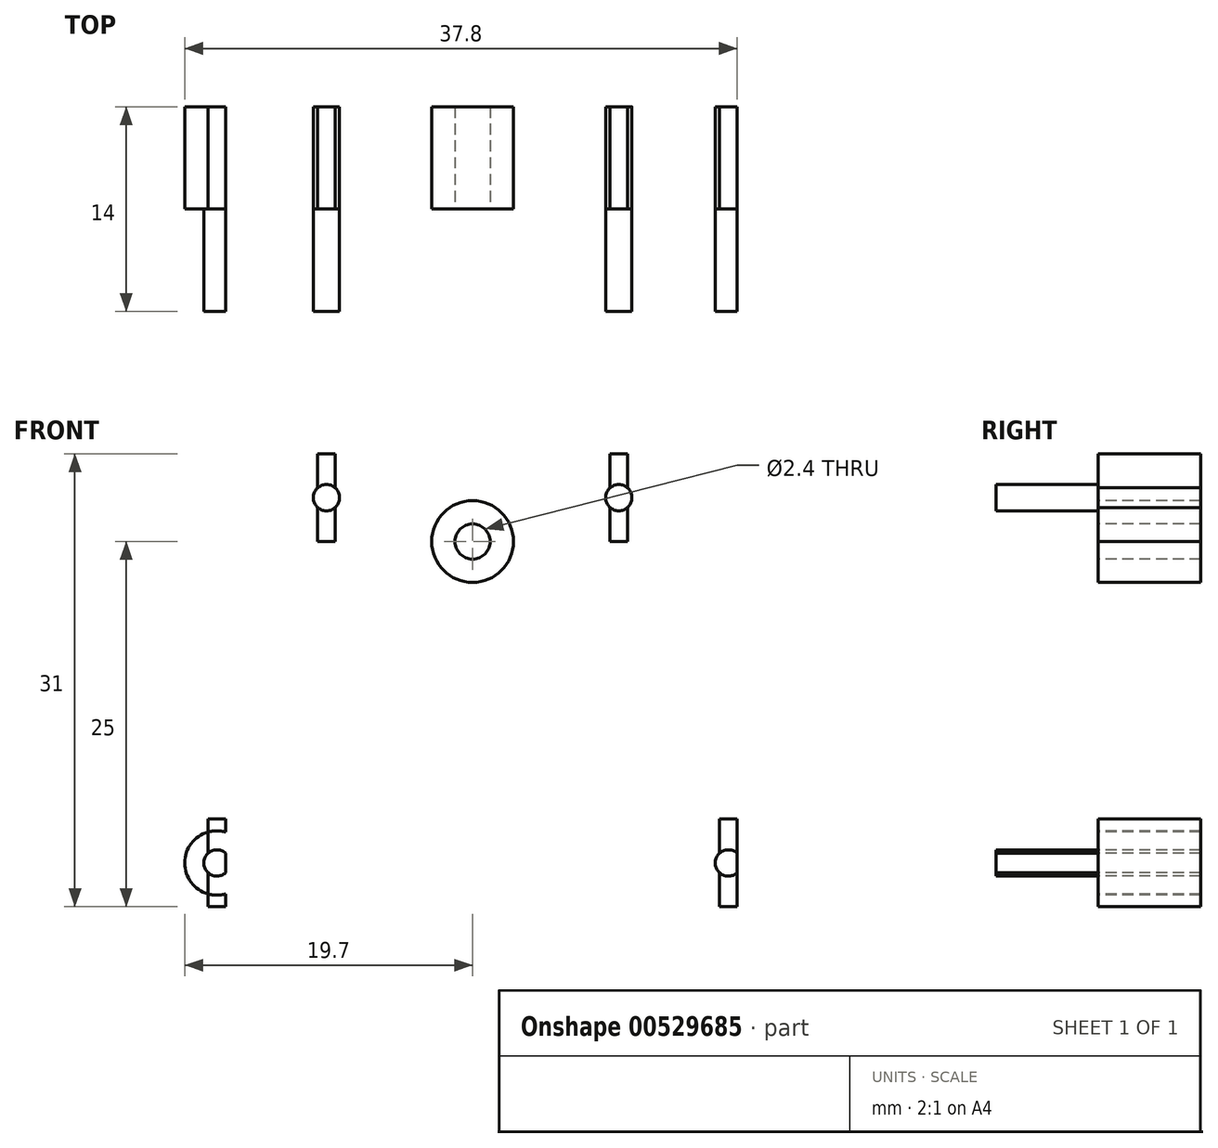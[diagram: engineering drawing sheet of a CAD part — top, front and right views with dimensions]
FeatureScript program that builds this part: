
annotation { "Feature Type Name" : "Feature", "Feature Type Description" : "" }
export const myFeature = defineFeature(function(context is Context, id is Id, definition is map)
    precondition{}
    {
        {
            var Q0;
            Q0=qCreatedBy(makeId("Front.planeOp"),FACE);
            var sketch = newSketch(context, id + "F0", { "sketchPlane" : qUnion([Q0])});
            skLineSegment(sketch, "E0", {"start": v(7.5, 25) * mm, "end": v(27.5, 25) * mm, "construction": true});
            skLineSegment(sketch, "E1", {"start": v(0, 0) * mm, "end": v(35, 0) * mm, "construction": true});
            skLineSegment(sketch, "E2", {"start": v(35, 0) * mm, "end": v(27.5, 25) * mm, "construction": true});
            skLineSegment(sketch, "E3", {"start": v(7.5, 25) * mm, "end": v(0, 0) * mm, "construction": true});
            skLineSegment(sketch, "E4", {"start": v(17.5, 25) * mm, "end": v(17.5, 0) * mm, "construction": true});
            skPoint(sketch, "E4.endSnap0", {"position": v(17.5, 0) * mm});
            skCircle(sketch, "E5", {"center": v(7.5, 25) * mm, "radius": 0.9 * mm});
            skCircle(sketch, "E6", {"center": v(27.5, 25) * mm, "radius": 0.9 * mm});
            skCircle(sketch, "E7", {"center": v(35, 0) * mm, "radius": 0.9 * mm});
            skCircle(sketch, "E8", {"center": v(0, 0) * mm, "radius": 0.9 * mm});
            skCircle(sketch, "E9", {"center": v(17.5, 22) * mm, "radius": 1.2 * mm});
            skCircle(sketch, "E10", {"center": v(17.5, 22) * mm, "radius": 2.8 * mm});
            skLineSegment(sketch, "E11.bottom", {"start": v(8.1, 22) * mm, "end": v(6.9, 22) * mm});
            skLineSegment(sketch, "E11.top", {"start": v(8.1, 28) * mm, "end": v(6.9, 28) * mm});
            skLineSegment(sketch, "E11.left", {"start": v(8.1, 22) * mm, "end": v(8.1, 28) * mm});
            skLineSegment(sketch, "E11.right", {"start": v(6.9, 22) * mm, "end": v(6.9, 28) * mm});
            skLineSegment(sketch, "E12.bottom", {"start": v(28.1, 22) * mm, "end": v(26.9, 22) * mm});
            skLineSegment(sketch, "E12.top", {"start": v(28.1, 28) * mm, "end": v(26.9, 28) * mm});
            skLineSegment(sketch, "E12.left", {"start": v(28.1, 22) * mm, "end": v(28.1, 28) * mm});
            skLineSegment(sketch, "E12.right", {"start": v(26.9, 22) * mm, "end": v(26.9, 28) * mm});
            skLineSegment(sketch, "E13.bottom", {"start": v(35.6, 3) * mm, "end": v(34.4, 3) * mm});
            skLineSegment(sketch, "E13.top", {"start": v(35.6, -3) * mm, "end": v(34.4, -3) * mm});
            skLineSegment(sketch, "E13.left", {"start": v(35.6, 3) * mm, "end": v(35.6, -3) * mm});
            skLineSegment(sketch, "E13.right", {"start": v(34.4, 3) * mm, "end": v(34.4, -3) * mm});
            skLineSegment(sketch, "E14.bottom", {"start": v(-0.6, 3) * mm, "end": v(0.6, 3) * mm});
            skLineSegment(sketch, "E14.top", {"start": v(-0.6, -3) * mm, "end": v(0.6, -3) * mm});
            skLineSegment(sketch, "E14.left", {"start": v(-0.6, 3) * mm, "end": v(-0.6, -3) * mm});
            skLineSegment(sketch, "E14.right", {"start": v(0.6, 3) * mm, "end": v(0.6, -3) * mm});
            skPoint(sketch, "E14.cornerSnap0", {"position": v(35, 3) * mm});
            skCircle(sketch, "E15", {"center": v(7.5, 25) * mm, "radius": 2.2 * mm});
            skCircle(sketch, "E16", {"center": v(27.5, 25) * mm, "radius": 2.2 * mm});
            skCircle(sketch, "E17", {"center": v(35, 0) * mm, "radius": 2.2 * mm});
            skCircle(sketch, "E18", {"center": v(0, 0) * mm, "radius": 2.2 * mm});
            skCircle(sketch, "E19", {"center": v(17.5, 4) * mm, "radius": 0.6 * mm});
            skSolve(sketch);
        }
        {
            var Q0;
            {var subQ0=sQuery(id+"F0.wireOp",EDGE,"E11.right");var subQ1=sQuery(id+"F0.wireOp",EDGE,"E5");var subQ2=makeQuery(id+"F0.imprint","INTERSECT",VERTEX,{"disambiguationData":[OD(0.0)],"derivedFrom":[subQ1,subQ0]});Q0=makeQuery(id+"F0.imprint","IMPRINT",FACE,{"disambiguationData":[TD([[makeQuery(id+"F0.imprint","IMPRINT",EDGE,{"disambiguationData":[TD([[subQ2,1.0]])],"derivedFrom":subQ1}),1.0]])]});}
            var Q1;
            {var subQ0=sQuery(id+"F0.wireOp",EDGE,"E11.right");var subQ1=sQuery(id+"F0.wireOp",EDGE,"E5");var subQ2=makeQuery(id+"F0.imprint","INTERSECT",VERTEX,{"disambiguationData":[OD(0.0)],"derivedFrom":[subQ1,subQ0]});Q1=makeQuery(id+"F0.imprint","IMPRINT",FACE,{"disambiguationData":[TD([[makeQuery(id+"F0.imprint","IMPRINT",EDGE,{"disambiguationData":[TD([[subQ2,-1.0]])],"derivedFrom":subQ1}),1.0]])]});}
            var Q2;
            {var subQ0=sQuery(id+"F0.wireOp",EDGE,"E11.left");var subQ1=sQuery(id+"F0.wireOp",EDGE,"E5");var subQ2=makeQuery(id+"F0.imprint","INTERSECT",VERTEX,{"disambiguationData":[OD(0.0)],"derivedFrom":[subQ1,subQ0]});Q2=makeQuery(id+"F0.imprint","IMPRINT",FACE,{"disambiguationData":[TD([[makeQuery(id+"F0.imprint","IMPRINT",EDGE,{"disambiguationData":[TD([[subQ2,1.0]])],"derivedFrom":subQ1}),1.0]])]});}
            var Q3;
            {var subQ0=sQuery(id+"F0.wireOp",EDGE,"E12.right");var subQ1=sQuery(id+"F0.wireOp",EDGE,"E6");var subQ2=makeQuery(id+"F0.imprint","INTERSECT",VERTEX,{"disambiguationData":[OD(0.0)],"derivedFrom":[subQ1,subQ0]});Q3=makeQuery(id+"F0.imprint","IMPRINT",FACE,{"disambiguationData":[TD([[makeQuery(id+"F0.imprint","IMPRINT",EDGE,{"disambiguationData":[TD([[subQ2,1.0]])],"derivedFrom":subQ1}),1.0]])]});}
            var Q4;
            {var subQ0=sQuery(id+"F0.wireOp",EDGE,"E12.right");var subQ1=sQuery(id+"F0.wireOp",EDGE,"E6");var subQ2=makeQuery(id+"F0.imprint","INTERSECT",VERTEX,{"disambiguationData":[OD(0.0)],"derivedFrom":[subQ1,subQ0]});Q4=makeQuery(id+"F0.imprint","IMPRINT",FACE,{"disambiguationData":[TD([[makeQuery(id+"F0.imprint","IMPRINT",EDGE,{"disambiguationData":[TD([[subQ2,-1.0]])],"derivedFrom":subQ1}),1.0]])]});}
            var Q5;
            {var subQ0=sQuery(id+"F0.wireOp",EDGE,"E12.left");var subQ1=sQuery(id+"F0.wireOp",EDGE,"E6");var subQ2=makeQuery(id+"F0.imprint","INTERSECT",VERTEX,{"disambiguationData":[OD(0.0)],"derivedFrom":[subQ1,subQ0]});Q5=makeQuery(id+"F0.imprint","IMPRINT",FACE,{"disambiguationData":[TD([[makeQuery(id+"F0.imprint","IMPRINT",EDGE,{"disambiguationData":[TD([[subQ2,1.0]])],"derivedFrom":subQ1}),1.0]])]});}
            var Q6;
            {var subQ0=sQuery(id+"F0.wireOp",EDGE,"E13.right");var subQ1=sQuery(id+"F0.wireOp",EDGE,"E7");var subQ2=makeQuery(id+"F0.imprint","INTERSECT",VERTEX,{"disambiguationData":[OD(0.0)],"derivedFrom":[subQ1,subQ0]});Q6=makeQuery(id+"F0.imprint","IMPRINT",FACE,{"disambiguationData":[TD([[makeQuery(id+"F0.imprint","IMPRINT",EDGE,{"disambiguationData":[TD([[subQ2,1.0]])],"derivedFrom":subQ1}),1.0]])]});}
            var Q7;
            {var subQ0=sQuery(id+"F0.wireOp",EDGE,"E13.left");var subQ1=sQuery(id+"F0.wireOp",EDGE,"E7");var subQ2=makeQuery(id+"F0.imprint","INTERSECT",VERTEX,{"disambiguationData":[OD(0.0)],"derivedFrom":[subQ1,subQ0]});Q7=makeQuery(id+"F0.imprint","IMPRINT",FACE,{"disambiguationData":[TD([[makeQuery(id+"F0.imprint","IMPRINT",EDGE,{"disambiguationData":[TD([[subQ2,1.0]])],"derivedFrom":subQ1}),1.0]])]});}
            var Q8;
            {var subQ0=sQuery(id+"F0.wireOp",EDGE,"E13.right");var subQ1=sQuery(id+"F0.wireOp",EDGE,"E7");var subQ2=makeQuery(id+"F0.imprint","INTERSECT",VERTEX,{"disambiguationData":[OD(0.0)],"derivedFrom":[subQ1,subQ0]});Q8=makeQuery(id+"F0.imprint","IMPRINT",FACE,{"disambiguationData":[TD([[makeQuery(id+"F0.imprint","IMPRINT",EDGE,{"disambiguationData":[TD([[subQ2,-1.0]])],"derivedFrom":subQ1}),1.0]])]});}
            var Q9;
            {var subQ0=sQuery(id+"F0.wireOp",EDGE,"E14.left");var subQ1=sQuery(id+"F0.wireOp",EDGE,"E8");var subQ2=makeQuery(id+"F0.imprint","INTERSECT",VERTEX,{"disambiguationData":[OD(0.0)],"derivedFrom":[subQ1,subQ0]});Q9=makeQuery(id+"F0.imprint","IMPRINT",FACE,{"disambiguationData":[TD([[makeQuery(id+"F0.imprint","IMPRINT",EDGE,{"disambiguationData":[TD([[subQ2,-1.0]])],"derivedFrom":subQ1}),1.0]])]});}
            var Q10;
            {var subQ0=sQuery(id+"F0.wireOp",EDGE,"E14.left");var subQ1=sQuery(id+"F0.wireOp",EDGE,"E8");var subQ2=makeQuery(id+"F0.imprint","INTERSECT",VERTEX,{"disambiguationData":[OD(0.0)],"derivedFrom":[subQ1,subQ0]});Q10=makeQuery(id+"F0.imprint","IMPRINT",FACE,{"disambiguationData":[TD([[makeQuery(id+"F0.imprint","IMPRINT",EDGE,{"disambiguationData":[TD([[subQ2,1.0]])],"derivedFrom":subQ1}),1.0]])]});}
            var Q11;
            {var subQ0=sQuery(id+"F0.wireOp",EDGE,"E14.right");var subQ1=sQuery(id+"F0.wireOp",EDGE,"E8");var subQ2=makeQuery(id+"F0.imprint","INTERSECT",VERTEX,{"disambiguationData":[OD(0.0)],"derivedFrom":[subQ1,subQ0]});Q11=makeQuery(id+"F0.imprint","IMPRINT",FACE,{"disambiguationData":[TD([[makeQuery(id+"F0.imprint","IMPRINT",EDGE,{"disambiguationData":[TD([[subQ2,1.0]])],"derivedFrom":subQ1}),1.0]])]});}
            extrude(context, id + "F1", {"entities" : qUnion([Q0, Q1, Q2, Q3, Q4, Q5, Q6, Q7, Q8, Q9, Q10, Q11]), "depth" : 7 * mm, "offsetDistance" : 25 * mm});
        }
        {
            var Q0;
            Q0=makeQuery(id+"F0.imprint","IMPRINT",FACE,{"disambiguationData":[TD([[makeQuery(id+"F0.imprint","IMPRINT",EDGE,{"derivedFrom":sQuery(id+"F0.wireOp",EDGE,"E9")}),-1.0]])]});
            var Q1;
            {var subQ0=sQuery(id+"F0.wireOp",EDGE,"E11.top");Q1=makeQuery(id+"F0.imprint","IMPRINT",FACE,{"disambiguationData":[TD([[makeQuery(id+"F0.imprint","IMPRINT",EDGE,{"derivedFrom":subQ0}),1.0]])]});}
            var Q2;
            {var subQ0=sQuery(id+"F0.wireOp",EDGE,"E11.right");var subQ1=sQuery(id+"F0.wireOp",EDGE,"E5");var subQ2=makeQuery(id+"F0.imprint","INTERSECT",VERTEX,{"disambiguationData":[OD(0.0)],"derivedFrom":[subQ1,subQ0]});Q2=makeQuery(id+"F0.imprint","IMPRINT",FACE,{"disambiguationData":[TD([[makeQuery(id+"F0.imprint","IMPRINT",EDGE,{"disambiguationData":[TD([[subQ2,1.0]])],"derivedFrom":subQ1}),-1.0]])]});}
            var Q3;
            {var subQ0=sQuery(id+"F0.wireOp",EDGE,"E11.right");var subQ1=sQuery(id+"F0.wireOp",EDGE,"E5");var subQ2=makeQuery(id+"F0.imprint","INTERSECT",VERTEX,{"disambiguationData":[OD(1.0)],"derivedFrom":[subQ1,subQ0]});Q3=makeQuery(id+"F0.imprint","IMPRINT",FACE,{"disambiguationData":[TD([[makeQuery(id+"F0.imprint","IMPRINT",EDGE,{"disambiguationData":[TD([[subQ2,-1.0]])],"derivedFrom":subQ1}),-1.0]])]});}
            var Q4;
            {var subQ0=sQuery(id+"F0.wireOp",EDGE,"E11.left");var subQ1=sQuery(id+"F0.wireOp",EDGE,"E5");var subQ2=makeQuery(id+"F0.imprint","INTERSECT",VERTEX,{"disambiguationData":[OD(0.0)],"derivedFrom":[subQ1,subQ0]});Q4=makeQuery(id+"F0.imprint","IMPRINT",FACE,{"disambiguationData":[TD([[makeQuery(id+"F0.imprint","IMPRINT",EDGE,{"disambiguationData":[TD([[subQ2,1.0]])],"derivedFrom":subQ1}),1.0]])]});}
            var Q5;
            {var subQ0=sQuery(id+"F0.wireOp",EDGE,"E12.right");var subQ1=sQuery(id+"F0.wireOp",EDGE,"E6");var subQ2=makeQuery(id+"F0.imprint","INTERSECT",VERTEX,{"disambiguationData":[OD(1.0)],"derivedFrom":[subQ1,subQ0]});Q5=makeQuery(id+"F0.imprint","IMPRINT",FACE,{"disambiguationData":[TD([[makeQuery(id+"F0.imprint","IMPRINT",EDGE,{"disambiguationData":[TD([[subQ2,-1.0]])],"derivedFrom":subQ1}),-1.0]])]});}
            var Q6;
            {var subQ0=sQuery(id+"F0.wireOp",EDGE,"E12.bottom");Q6=makeQuery(id+"F0.imprint","IMPRINT",FACE,{"disambiguationData":[TD([[makeQuery(id+"F0.imprint","IMPRINT",EDGE,{"derivedFrom":subQ0}),-1.0]])]});}
            var Q7;
            {var subQ0=sQuery(id+"F0.wireOp",EDGE,"E12.right");var subQ1=sQuery(id+"F0.wireOp",EDGE,"E6");var subQ2=makeQuery(id+"F0.imprint","INTERSECT",VERTEX,{"disambiguationData":[OD(0.0)],"derivedFrom":[subQ1,subQ0]});Q7=makeQuery(id+"F0.imprint","IMPRINT",FACE,{"disambiguationData":[TD([[makeQuery(id+"F0.imprint","IMPRINT",EDGE,{"disambiguationData":[TD([[subQ2,1.0]])],"derivedFrom":subQ1}),-1.0]])]});}
            var Q8;
            {var subQ0=sQuery(id+"F0.wireOp",EDGE,"E12.right");var subQ1=sQuery(id+"F0.wireOp",EDGE,"E6");var subQ2=makeQuery(id+"F0.imprint","INTERSECT",VERTEX,{"disambiguationData":[OD(0.0)],"derivedFrom":[subQ1,subQ0]});Q8=makeQuery(id+"F0.imprint","IMPRINT",FACE,{"disambiguationData":[TD([[makeQuery(id+"F0.imprint","IMPRINT",EDGE,{"disambiguationData":[TD([[subQ2,1.0]])],"derivedFrom":subQ1}),1.0]])]});}
            var Q9;
            {var subQ0=sQuery(id+"F0.wireOp",EDGE,"E12.left");var subQ1=sQuery(id+"F0.wireOp",EDGE,"E6");var subQ2=makeQuery(id+"F0.imprint","INTERSECT",VERTEX,{"disambiguationData":[OD(0.0)],"derivedFrom":[subQ1,subQ0]});Q9=makeQuery(id+"F0.imprint","IMPRINT",FACE,{"disambiguationData":[TD([[makeQuery(id+"F0.imprint","IMPRINT",EDGE,{"disambiguationData":[TD([[subQ2,1.0]])],"derivedFrom":subQ1}),1.0]])]});}
            var Q10;
            {var subQ0=sQuery(id+"F0.wireOp",EDGE,"E12.right");var subQ1=sQuery(id+"F0.wireOp",EDGE,"E6");var subQ2=makeQuery(id+"F0.imprint","INTERSECT",VERTEX,{"disambiguationData":[OD(0.0)],"derivedFrom":[subQ1,subQ0]});Q10=makeQuery(id+"F0.imprint","IMPRINT",FACE,{"disambiguationData":[TD([[makeQuery(id+"F0.imprint","IMPRINT",EDGE,{"disambiguationData":[TD([[subQ2,-1.0]])],"derivedFrom":subQ1}),1.0]])]});}
            var Q11;
            {var subQ0=sQuery(id+"F0.wireOp",EDGE,"E11.right");var subQ1=sQuery(id+"F0.wireOp",EDGE,"E5");var subQ2=makeQuery(id+"F0.imprint","INTERSECT",VERTEX,{"disambiguationData":[OD(0.0)],"derivedFrom":[subQ1,subQ0]});Q11=makeQuery(id+"F0.imprint","IMPRINT",FACE,{"disambiguationData":[TD([[makeQuery(id+"F0.imprint","IMPRINT",EDGE,{"disambiguationData":[TD([[subQ2,1.0]])],"derivedFrom":subQ1}),1.0]])]});}
            var Q12;
            {var subQ0=sQuery(id+"F0.wireOp",EDGE,"E11.right");var subQ1=sQuery(id+"F0.wireOp",EDGE,"E5");var subQ2=makeQuery(id+"F0.imprint","INTERSECT",VERTEX,{"disambiguationData":[OD(0.0)],"derivedFrom":[subQ1,subQ0]});Q12=makeQuery(id+"F0.imprint","IMPRINT",FACE,{"disambiguationData":[TD([[makeQuery(id+"F0.imprint","IMPRINT",EDGE,{"disambiguationData":[TD([[subQ2,-1.0]])],"derivedFrom":subQ1}),1.0]])]});}
            var Q13;
            {var subQ0=sQuery(id+"F0.wireOp",EDGE,"E14.bottom");Q13=makeQuery(id+"F0.imprint","IMPRINT",FACE,{"disambiguationData":[TD([[makeQuery(id+"F0.imprint","IMPRINT",EDGE,{"derivedFrom":subQ0}),-1.0]])]});}
            var Q14;
            {var subQ0=sQuery(id+"F0.wireOp",EDGE,"E14.left");var subQ1=sQuery(id+"F0.wireOp",EDGE,"E8");var subQ2=makeQuery(id+"F0.imprint","INTERSECT",VERTEX,{"disambiguationData":[OD(0.0)],"derivedFrom":[subQ1,subQ0]});Q14=makeQuery(id+"F0.imprint","IMPRINT",FACE,{"disambiguationData":[TD([[makeQuery(id+"F0.imprint","IMPRINT",EDGE,{"disambiguationData":[TD([[subQ2,1.0]])],"derivedFrom":subQ1}),-1.0]])]});}
            var Q15;
            {var subQ0=sQuery(id+"F0.wireOp",EDGE,"E14.left");var subQ1=sQuery(id+"F0.wireOp",EDGE,"E8");var subQ2=makeQuery(id+"F0.imprint","INTERSECT",VERTEX,{"disambiguationData":[OD(1.0)],"derivedFrom":[subQ1,subQ0]});Q15=makeQuery(id+"F0.imprint","IMPRINT",FACE,{"disambiguationData":[TD([[makeQuery(id+"F0.imprint","IMPRINT",EDGE,{"disambiguationData":[TD([[subQ2,-1.0]])],"derivedFrom":subQ1}),-1.0]])]});}
            var Q16;
            {var subQ0=sQuery(id+"F0.wireOp",EDGE,"E14.top");Q16=makeQuery(id+"F0.imprint","IMPRINT",FACE,{"disambiguationData":[TD([[makeQuery(id+"F0.imprint","IMPRINT",EDGE,{"derivedFrom":subQ0}),1.0]])]});}
            var Q17;
            {var subQ0=sQuery(id+"F0.wireOp",EDGE,"E13.bottom");Q17=makeQuery(id+"F0.imprint","IMPRINT",FACE,{"disambiguationData":[TD([[makeQuery(id+"F0.imprint","IMPRINT",EDGE,{"derivedFrom":subQ0}),1.0]])]});}
            var Q18;
            {var subQ0=sQuery(id+"F0.wireOp",EDGE,"E13.right");var subQ1=sQuery(id+"F0.wireOp",EDGE,"E7");var subQ2=makeQuery(id+"F0.imprint","INTERSECT",VERTEX,{"disambiguationData":[OD(0.0)],"derivedFrom":[subQ1,subQ0]});Q18=makeQuery(id+"F0.imprint","IMPRINT",FACE,{"disambiguationData":[TD([[makeQuery(id+"F0.imprint","IMPRINT",EDGE,{"disambiguationData":[TD([[subQ2,1.0]])],"derivedFrom":subQ1}),-1.0]])]});}
            var Q19;
            {var subQ0=sQuery(id+"F0.wireOp",EDGE,"E13.right");var subQ1=sQuery(id+"F0.wireOp",EDGE,"E7");var subQ2=makeQuery(id+"F0.imprint","INTERSECT",VERTEX,{"disambiguationData":[OD(1.0)],"derivedFrom":[subQ1,subQ0]});Q19=makeQuery(id+"F0.imprint","IMPRINT",FACE,{"disambiguationData":[TD([[makeQuery(id+"F0.imprint","IMPRINT",EDGE,{"disambiguationData":[TD([[subQ2,-1.0]])],"derivedFrom":subQ1}),-1.0]])]});}
            var Q20;
            {var subQ0=sQuery(id+"F0.wireOp",EDGE,"E13.top");Q20=makeQuery(id+"F0.imprint","IMPRINT",FACE,{"disambiguationData":[TD([[makeQuery(id+"F0.imprint","IMPRINT",EDGE,{"derivedFrom":subQ0}),-1.0]])]});}
            var Q21;
            Q21=makeQuery(id+"F1.opExtrude","CAP_FACE",FACE,{"disambiguationData":[OSD([sQuery(id+"F0.wireOp",EDGE,"E7")])],"isStart":false});
            var Q22;
            {var subQ0=sQuery(id+"F0.wireOp",EDGE,"E12.top");Q22=makeQuery(id+"F0.imprint","IMPRINT",FACE,{"disambiguationData":[TD([[makeQuery(id+"F0.imprint","IMPRINT",EDGE,{"derivedFrom":subQ0}),1.0]])]});}
            var Q23;
            {var subQ0=sQuery(id+"F0.wireOp",EDGE,"E14.left");var subQ1=sQuery(id+"F0.wireOp",EDGE,"E8");var subQ2=makeQuery(id+"F0.imprint","INTERSECT",VERTEX,{"disambiguationData":[OD(0.0)],"derivedFrom":[subQ1,subQ0]});Q23=makeQuery(id+"F0.imprint","IMPRINT",FACE,{"disambiguationData":[TD([[makeQuery(id+"F0.imprint","IMPRINT",EDGE,{"disambiguationData":[TD([[subQ2,-1.0]])],"derivedFrom":subQ1}),1.0]])]});}
            var Q24;
            {var subQ0=sQuery(id+"F0.wireOp",EDGE,"E14.left");var subQ1=sQuery(id+"F0.wireOp",EDGE,"E8");var subQ2=makeQuery(id+"F0.imprint","INTERSECT",VERTEX,{"disambiguationData":[OD(0.0)],"derivedFrom":[subQ1,subQ0]});Q24=makeQuery(id+"F0.imprint","IMPRINT",FACE,{"disambiguationData":[TD([[makeQuery(id+"F0.imprint","IMPRINT",EDGE,{"disambiguationData":[TD([[subQ2,1.0]])],"derivedFrom":subQ1}),1.0]])]});}
            var Q25;
            {var subQ0=sQuery(id+"F0.wireOp",EDGE,"E14.right");var subQ1=sQuery(id+"F0.wireOp",EDGE,"E8");var subQ2=makeQuery(id+"F0.imprint","INTERSECT",VERTEX,{"disambiguationData":[OD(0.0)],"derivedFrom":[subQ1,subQ0]});Q25=makeQuery(id+"F0.imprint","IMPRINT",FACE,{"disambiguationData":[TD([[makeQuery(id+"F0.imprint","IMPRINT",EDGE,{"disambiguationData":[TD([[subQ2,1.0]])],"derivedFrom":subQ1}),1.0]])]});}
            var Q26;
            {var subQ0=sQuery(id+"F0.wireOp",EDGE,"E13.right");var subQ1=sQuery(id+"F0.wireOp",EDGE,"E7");var subQ2=makeQuery(id+"F0.imprint","INTERSECT",VERTEX,{"disambiguationData":[OD(0.0)],"derivedFrom":[subQ1,subQ0]});Q26=makeQuery(id+"F0.imprint","IMPRINT",FACE,{"disambiguationData":[TD([[makeQuery(id+"F0.imprint","IMPRINT",EDGE,{"disambiguationData":[TD([[subQ2,-1.0]])],"derivedFrom":subQ1}),1.0]])]});}
            var Q27;
            {var subQ0=sQuery(id+"F0.wireOp",EDGE,"E13.right");var subQ1=sQuery(id+"F0.wireOp",EDGE,"E7");var subQ2=makeQuery(id+"F0.imprint","INTERSECT",VERTEX,{"disambiguationData":[OD(0.0)],"derivedFrom":[subQ1,subQ0]});Q27=makeQuery(id+"F0.imprint","IMPRINT",FACE,{"disambiguationData":[TD([[makeQuery(id+"F0.imprint","IMPRINT",EDGE,{"disambiguationData":[TD([[subQ2,1.0]])],"derivedFrom":subQ1}),1.0]])]});}
            var Q28;
            {var subQ0=sQuery(id+"F0.wireOp",EDGE,"E13.left");var subQ1=sQuery(id+"F0.wireOp",EDGE,"E7");var subQ2=makeQuery(id+"F0.imprint","INTERSECT",VERTEX,{"disambiguationData":[OD(0.0)],"derivedFrom":[subQ1,subQ0]});Q28=makeQuery(id+"F0.imprint","IMPRINT",FACE,{"disambiguationData":[TD([[makeQuery(id+"F0.imprint","IMPRINT",EDGE,{"disambiguationData":[TD([[subQ2,1.0]])],"derivedFrom":subQ1}),1.0]])]});}
            var Q29;
            {var subQ0=sQuery(id+"F0.wireOp",EDGE,"E11.bottom");Q29=makeQuery(id+"F0.imprint","IMPRINT",FACE,{"disambiguationData":[TD([[makeQuery(id+"F0.imprint","IMPRINT",EDGE,{"derivedFrom":subQ0}),-1.0]])]});}
            extrude(context, id + "F2", {"entities" : qUnion([Q0, Q1, Q2, Q3, Q4, Q5, Q6, Q7, Q8, Q9, Q10, Q11, Q12, Q13, Q14, Q15, Q16, Q17, Q18, Q19, Q20, Q21, Q22, Q23, Q24, Q25, Q26, Q27, Q28, Q29]), "oppositeDirection" : true, "depth" : 7 * mm, "offsetDistance" : 25 * mm});
        }
    });
